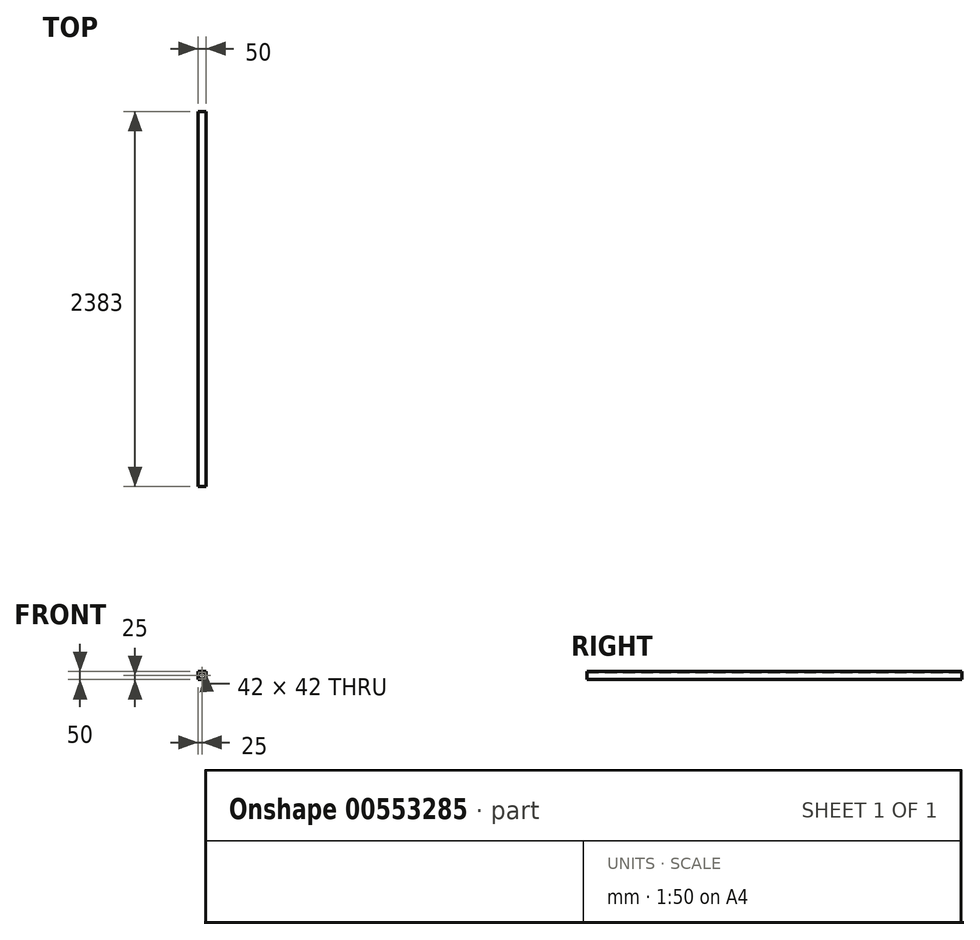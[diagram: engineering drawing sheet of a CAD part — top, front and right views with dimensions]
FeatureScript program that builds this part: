
annotation { "Feature Type Name" : "Feature", "Feature Type Description" : "" }
export const myFeature = defineFeature(function(context is Context, id is Id, definition is map)
    precondition{}
    {
        {
            var Q0;
            Q0=qCreatedBy(makeId("Front.planeOp"),FACE);
            var sketch = newSketch(context, id + "F0", { "sketchPlane" : qUnion([Q0])});
            skLineSegment(sketch, "E0.bottom", {"start": v(-25, -25) * mm, "end": v(25, -25) * mm});
            skLineSegment(sketch, "E0.top", {"start": v(-25, 25) * mm, "end": v(25, 25) * mm});
            skLineSegment(sketch, "E0.left", {"start": v(-25, -25) * mm, "end": v(-25, 25) * mm});
            skLineSegment(sketch, "E0.right", {"start": v(25, -25) * mm, "end": v(25, 25) * mm});
            skPoint(sketch, "E0.middle", {"position": v(0, 0) * mm});
            skLineSegment(sketch, "E1.bottom", {"start": v(-21, -21) * mm, "end": v(21, -21) * mm});
            skLineSegment(sketch, "E1.top", {"start": v(-21, 21) * mm, "end": v(21, 21) * mm});
            skLineSegment(sketch, "E1.left", {"start": v(-21, -21) * mm, "end": v(-21, 21) * mm});
            skLineSegment(sketch, "E1.right", {"start": v(21, -21) * mm, "end": v(21, 21) * mm});
            skSolve(sketch);
        }
        {
            var Q0;
            Q0=makeQuery(id+"F0.imprint","IMPRINT",FACE,{"disambiguationData":[TD([[makeQuery(id+"F0.imprint","IMPRINT",EDGE,{"derivedFrom":sQuery(id+"F0.wireOp",EDGE,"E0.bottom")}),1.0]])]});
            extrude(context, id + "F1", {"entities" : qUnion([Q0]), "depth" : 2383 * mm, "offsetDistance" : 25 * mm});
        }
    });
